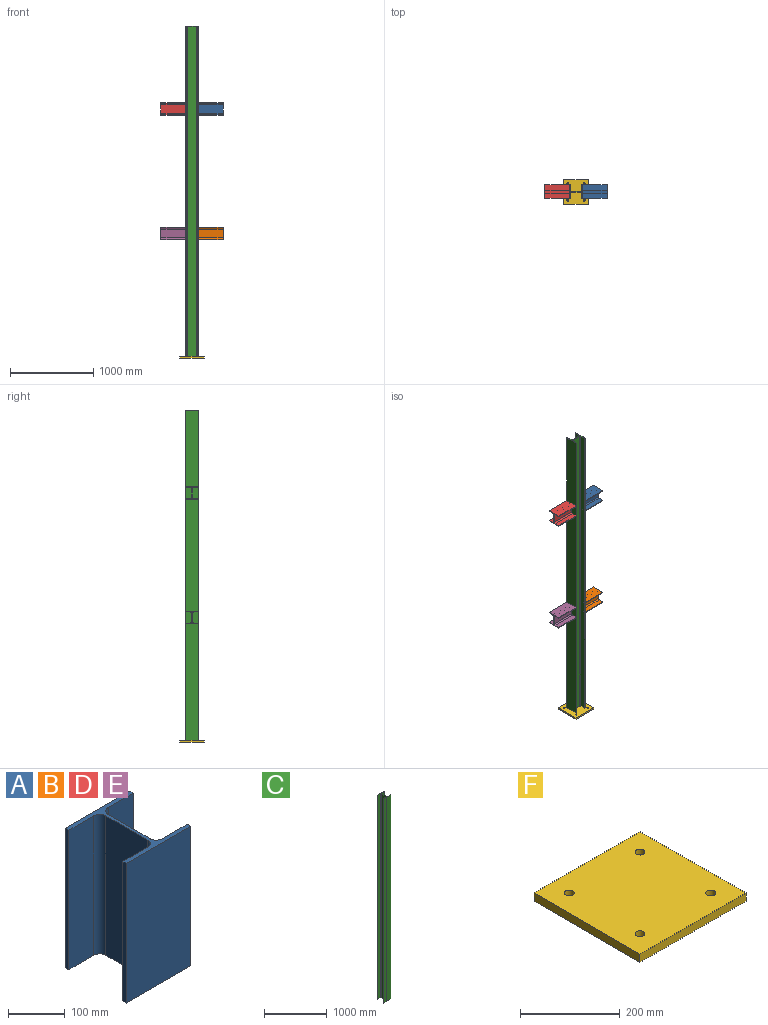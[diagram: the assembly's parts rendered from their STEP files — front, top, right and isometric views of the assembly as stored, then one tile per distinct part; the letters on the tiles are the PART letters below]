
ASSEMBLY  parts=6 mates=3
PART A: 18 faces, bbox 160x152x300 mm
  f0: plane 300x9mm, normal (-1,0,0), area 2700mm2, adj f1,f15,f16,f17
  f1: plane 300x62mm, normal (0,1,0), area 18600mm2, adj f0,f2,f16,f17
  f2: cylinder r=15mm len=300mm, axis (0,0,1), area 7068.6mm2, adj f1,f3,f16,f17
  f3: plane 300x104mm, normal (-1,0,0), area 31200mm2, adj f2,f4,f16,f17
  f4: cylinder r=15mm len=300mm, axis (0,0,1), area 7068.6mm2, adj f3,f5,f16,f17
  f5: plane 300x62mm, normal (0,-1,0), area 18600mm2, adj f4,f6,f16,f17
  f6: plane 300x9mm, normal (-1,0,0), area 2700mm2, adj f5,f7,f16,f17
  f7: plane 300x160mm, normal (0,1,0), area 48000mm2, adj f6,f8,f16,f17
  f8: plane 300x9mm, normal (1,0,0), area 2700mm2, adj f7,f9,f16,f17
  f9: plane 300x62mm, normal (0,-1,0), area 18600mm2, adj f8,f10,f16,f17
  f10: cylinder r=15mm len=300mm, axis (0,0,1), area 7068.6mm2, adj f9,f11,f16,f17
  f11: plane 300x104mm, normal (1,0,0), area 31200mm2, adj f10,f12,f16,f17
  f12: cylinder r=15mm len=300mm, axis (0,0,1), area 7068.6mm2, adj f11,f13,f16,f17
  f13: plane 300x62mm, normal (0,1,0), area 18600mm2, adj f12,f14,f16,f17
  f14: plane 300x9mm, normal (1,0,0), area 2700mm2, adj f13,f15,f16,f17
  f15: plane 300x160mm, normal (0,-1,0), area 48000mm2, adj f0,f14,f16,f17
  f16: plane 160x152mm, normal (0,0,1), area 3877.1mm2, adj f0,f1,f2,f3,f4,f5,f6,f7
  f17: plane 160x152mm, normal (0,0,-1), area 3877.1mm2, adj f0,f1,f2,f3,f4,f5,f6,f7
PART B: same geometry as A
PART C: 18 faces, bbox 160x152x3980 mm
  f0: plane 3980x9mm, normal (-1,0,0), area 35820mm2, adj f1,f15,f16,f17
  f1: plane 3980x62mm, normal (0,1,0), area 246760mm2, adj f0,f2,f16,f17
  f2: cylinder r=15mm len=3980mm, axis (0,0,1), area 93776.5mm2, adj f1,f3,f16,f17
  f3: plane 3980x104mm, normal (-1,0,0), area 413920mm2, adj f2,f4,f16,f17
  f4: cylinder r=15mm len=3980mm, axis (0,0,1), area 93776.5mm2, adj f3,f5,f16,f17
  f5: plane 3980x62mm, normal (0,-1,0), area 246760mm2, adj f4,f6,f16,f17
  f6: plane 3980x9mm, normal (-1,0,0), area 35820mm2, adj f5,f7,f16,f17
  f7: plane 3980x160mm, normal (0,1,0), area 636800mm2, adj f6,f8,f16,f17
  f8: plane 3980x9mm, normal (1,0,0), area 35820mm2, adj f7,f9,f16,f17
  f9: plane 3980x62mm, normal (0,-1,0), area 246760mm2, adj f8,f10,f16,f17
  f10: cylinder r=15mm len=3980mm, axis (0,0,1), area 93776.5mm2, adj f9,f11,f16,f17
  f11: plane 3980x104mm, normal (1,0,0), area 413920mm2, adj f10,f12,f16,f17
  f12: cylinder r=15mm len=3980mm, axis (0,0,1), area 93776.5mm2, adj f11,f13,f16,f17
  f13: plane 3980x62mm, normal (0,1,0), area 246760mm2, adj f12,f14,f16,f17
  f14: plane 3980x9mm, normal (1,0,0), area 35820mm2, adj f13,f15,f16,f17
  f15: plane 3980x160mm, normal (0,-1,0), area 636800mm2, adj f0,f14,f16,f17
  f16: plane 160x152mm, normal (0,0,1), area 3877.1mm2, adj f0,f1,f2,f3,f4,f5,f6,f7
  f17: plane 160x152mm, normal (0,0,-1), area 3877.1mm2, adj f0,f1,f2,f3,f4,f5,f6,f7
PART D: same geometry as A
PART E: same geometry as A
PART F: 10 faces, bbox 300x300x20 mm
  f0: plane 300x20mm, normal (1,0,0), area 6000mm2, adj f1,f6,f8,f9
  f1: plane 300x20mm, normal (0,1,0), area 6000mm2, adj f0,f2,f8,f9
  f2: plane 300x20mm, normal (-1,0,0), area 6000mm2, adj f1,f6,f8,f9
  f3: cylinder r=10mm len=20mm, axis (0,0,-1), area 1256.6mm2, adj f8,f9
  f4: cylinder r=10mm len=20mm, axis (0,0,-1), area 1256.6mm2, adj f8,f9
  f5: cylinder r=10mm len=20mm, axis (0,0,-1), area 1256.6mm2, adj f8,f9
  f6: plane 300x20mm, normal (0,-1,0), area 6000mm2, adj f0,f2,f8,f9
  f7: cylinder r=10mm len=20mm, axis (0,0,-1), area 1256.6mm2, adj f8,f9
  f8: plane 300x300mm, normal (0,0,1), area 88743.4mm2, adj f0,f1,f2,f3,f4,f5,f6,f7
  f9: plane 300x300mm, normal (0,0,-1), area 88743.4mm2, adj f0,f1,f2,f3,f4,f5,f6,f7
PLACE A rot(axis=(0.58,0.58,0.58),120deg) t=(226,0,3000)mm
PLACE B rot(axis=(0.58,0.58,0.58),120deg) t=(226,0,1500)mm
PLACE C rot(axis=(0,0,1),90deg) t=(0,0,2010)mm
PLACE D rot(axis=(0.58,0.58,0.58),120deg) t=(-226,0,3000)mm
PLACE E rot(axis=(0.58,0.58,0.58),120deg) t=(-226,0,1500)mm
PLACE F at identity
MATE fastened C.f17 <-> F.f8  axis (0,0,-1) through (0,0,20)mm
MATE fastened B.f17 <-> C.f15  axis (-1,0,0) through (76,0,1500)mm
MATE fastened E.f16 <-> C.f7  axis (1,0,0) through (-76,0,1500)mm
